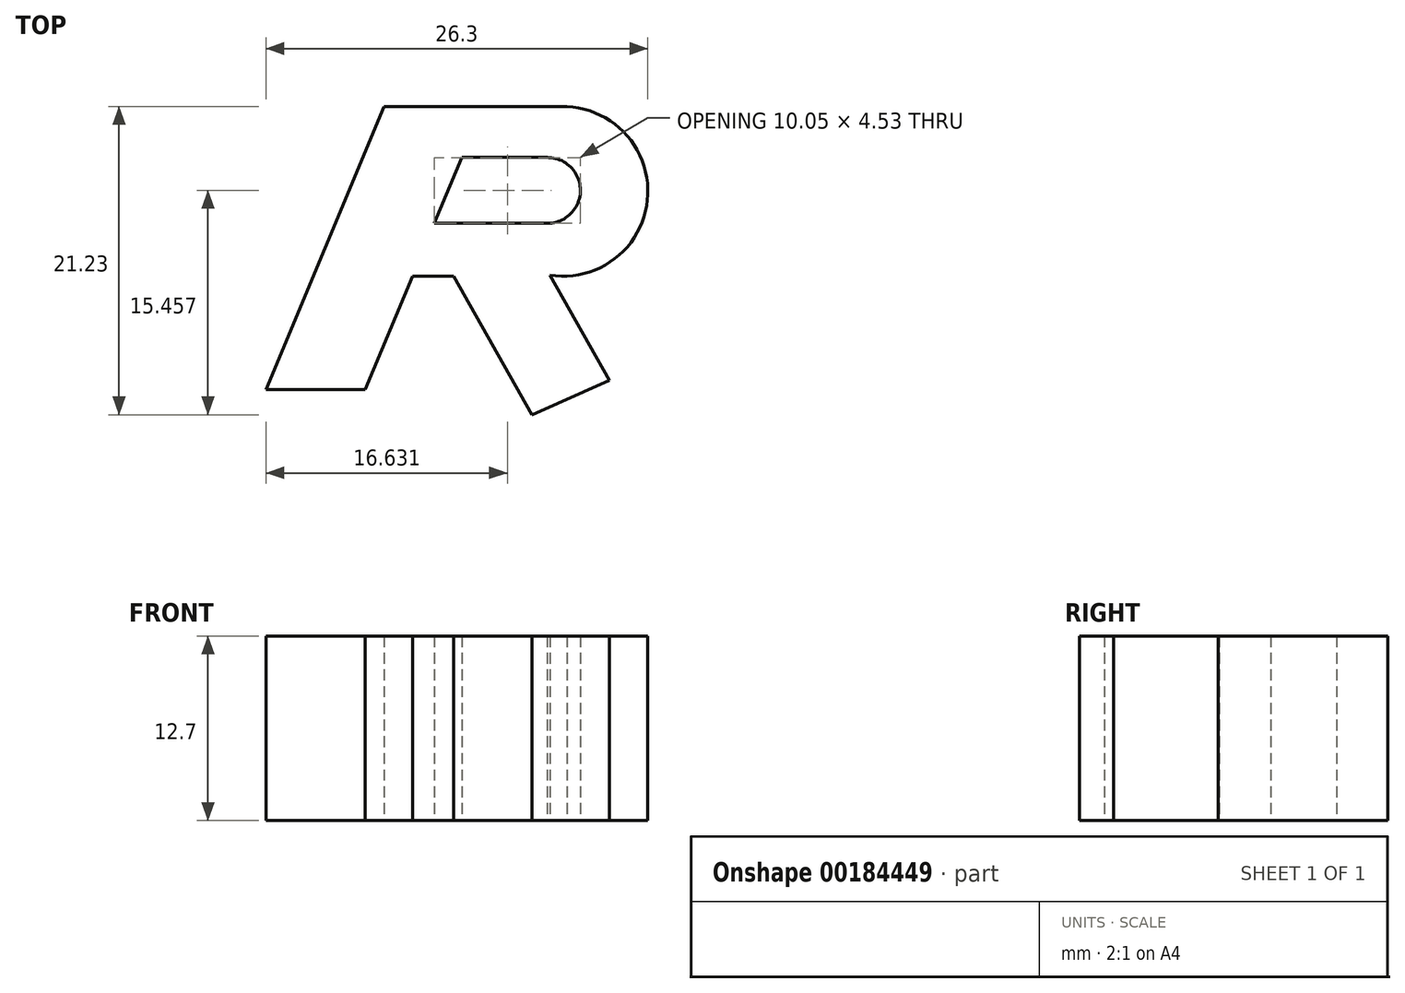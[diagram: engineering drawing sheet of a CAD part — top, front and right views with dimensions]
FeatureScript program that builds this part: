
annotation { "Feature Type Name" : "Feature", "Feature Type Description" : "" }
export const myFeature = defineFeature(function(context is Context, id is Id, definition is map)
    precondition{}
    {
        {
            var Q0;
            Q0=qCreatedBy(makeId("Top.planeOp"),FACE);
            var sketch = newSketch(context, id + "F0", { "sketchPlane" : qUnion([Q0])});
            skLineSegment(sketch, "E0", {"start": v(50.05, 11.4) * mm, "end": v(41.52, -9.11) * mm});
            skLineSegment(sketch, "E1", {"start": v(41.52, -9.11) * mm, "end": v(49.45, -9.11) * mm});
            skLineSegment(sketch, "E2", {"start": v(49.45, -9.11) * mm, "end": v(52.7, -1.3) * mm});
            skLineSegment(sketch, "E3", {"start": v(52.7, -1.3) * mm, "end": v(54.9, -1.3) * mm});
            skLineSegment(sketch, "E4", {"start": v(54.9, -1.3) * mm, "end": v(60.38, -10.98) * mm});
            skLineSegment(sketch, "E5", {"start": v(50.05, 11.4) * mm, "end": v(63.03, 11.4) * mm});
            skLineSegment(sketch, "E6.2", {"start": v(56.1, 6.89) * mm, "end": v(61.64, 6.89) * mm});
            skLineSegment(sketch, "E7", {"start": v(61.67, 3.37) * mm, "end": v(54.65, 3.37) * mm});
            skArc(sketch, "E8", {"start": v(61.67, 3.37) * mm, "mid": v(63.43, 5.14) * mm, "end": v(61.64, 6.89) * mm});
            skLineSegment(sketch, "E9", {"start": v(54.65, 3.37) * mm, "end": v(56.1, 6.89) * mm});
            skLineSegment(sketch, "E10", {"start": v(62.74, -1.3) * mm, "end": v(66.64, -8.21) * mm});
            skLineSegment(sketch, "E11", {"start": v(66.64, -8.21) * mm, "end": v(60.38, -10.98) * mm});
            skArc(sketch, "E12", {"start": v(62.74, -1.3) * mm, "mid": v(69.1, 4.91) * mm, "end": v(63.03, 11.4) * mm});
            skLineSegment(sketch, "E13.0", {"start": v(50.4, 10.9) * mm, "end": v(42.28, -8.6) * mm});
            skLineSegment(sketch, "E13.1", {"start": v(42.28, -8.6) * mm, "end": v(49.11, -8.6) * mm});
            skLineSegment(sketch, "E13.2", {"start": v(50.4, 10.9) * mm, "end": v(63.02, 10.9) * mm});
            skLineSegment(sketch, "E13.3", {"start": v(49.11, -8.6) * mm, "end": v(52.37, -0.79) * mm});
            skLineSegment(sketch, "E13.4", {"start": v(52.37, -0.79) * mm, "end": v(55.2, -0.79) * mm});
            skArc(sketch, "E13.5", {"start": v(61.82, -0.72) * mm, "mid": v(68.55, 4.46) * mm, "end": v(63.02, 10.9) * mm});
            skLineSegment(sketch, "E13.6", {"start": v(61.82, -0.72) * mm, "end": v(65.93, -7.97) * mm});
            skLineSegment(sketch, "E13.7", {"start": v(65.93, -7.97) * mm, "end": v(60.6, -10.33) * mm});
            skLineSegment(sketch, "E13.8", {"start": v(55.2, -0.79) * mm, "end": v(60.6, -10.33) * mm});
            skLineSegment(sketch, "E14.0", {"start": v(55.77, 7.4) * mm, "end": v(61.64, 7.4) * mm});
            skLineSegment(sketch, "E14.1", {"start": v(53.88, 2.86) * mm, "end": v(55.77, 7.4) * mm});
            skLineSegment(sketch, "E14.2", {"start": v(61.67, 2.86) * mm, "end": v(53.88, 2.86) * mm});
            skArc(sketch, "E14.3", {"start": v(61.67, 2.86) * mm, "mid": v(63.94, 5.14) * mm, "end": v(61.64, 7.4) * mm});
            skSolve(sketch);
        }
        {
            var Q0;
            {var subQ0=sQuery(id+"F0.wireOp",EDGE,"0WH1CMh5-IIct-Ghxc-y3FU-H90Uj8hS3lVa");Q0=makeQuery(id+"F0.imprint","IMPRINT",FACE,{"disambiguationData":[TD([[makeQuery(id+"F0.imprint","IMPRINT",EDGE,{"derivedFrom":subQ0}),1.0]])]});}
            var Q1;
            Q1=makeQuery(id+"F0.imprint","IMPRINT",FACE,{"disambiguationData":[TD([[makeQuery(id+"F0.imprint","IMPRINT",EDGE,{"derivedFrom":sQuery(id+"F0.wireOp",EDGE,"bNU62lUK-uF5p-bWZ0-EBHU-JxfuysNmUOex")}),-1.0]])]});
            var Q2;
            {var subQ1=sQuery(id+"F0.wireOp",EDGE,"N3sPrRag-mu5E-O2f5-6fvR-lNnh5q95kd9u");Q2=makeQuery(id+"F0.imprint","IMPRINT",FACE,{"disambiguationData":[TD([[makeQuery(id+"F0.imprint","IMPRINT",EDGE,{"derivedFrom":subQ1}),1.0]])]});}
            var Q3;
            Q3=makeQuery(id+"F0.imprint","IMPRINT",FACE,{"disambiguationData":[TD([[makeQuery(id+"F0.imprint","IMPRINT",EDGE,{"derivedFrom":sQuery(id+"F0.wireOp",EDGE,"ETaB8Tsc-dl5d-4Bpu-is8m-ihjGwD2GjhUy")}),1.0]])]});
            var Q4;
            Q4=makeQuery(id+"F0.imprint","IMPRINT",FACE,{"disambiguationData":[TD([[makeQuery(id+"F0.imprint","IMPRINT",EDGE,{"derivedFrom":sQuery(id+"F0.wireOp",EDGE,"QuCEtsMZ-SjIu-0d8u-tyjV-veN81ArypZlW")}),1.0]])]});
            var Q5;
            Q5=makeQuery(id+"F0.imprint","IMPRINT",FACE,{"disambiguationData":[TD([[makeQuery(id+"F0.imprint","IMPRINT",EDGE,{"derivedFrom":sQuery(id+"F0.wireOp",EDGE,"E13.0")}),1.0]])]});
            extrude(context, id + "F1", {"entities" : qUnion([Q0, Q1, Q2, Q3, Q4, Q5]), "depth" : 12.7 * mm});
        }
    });
